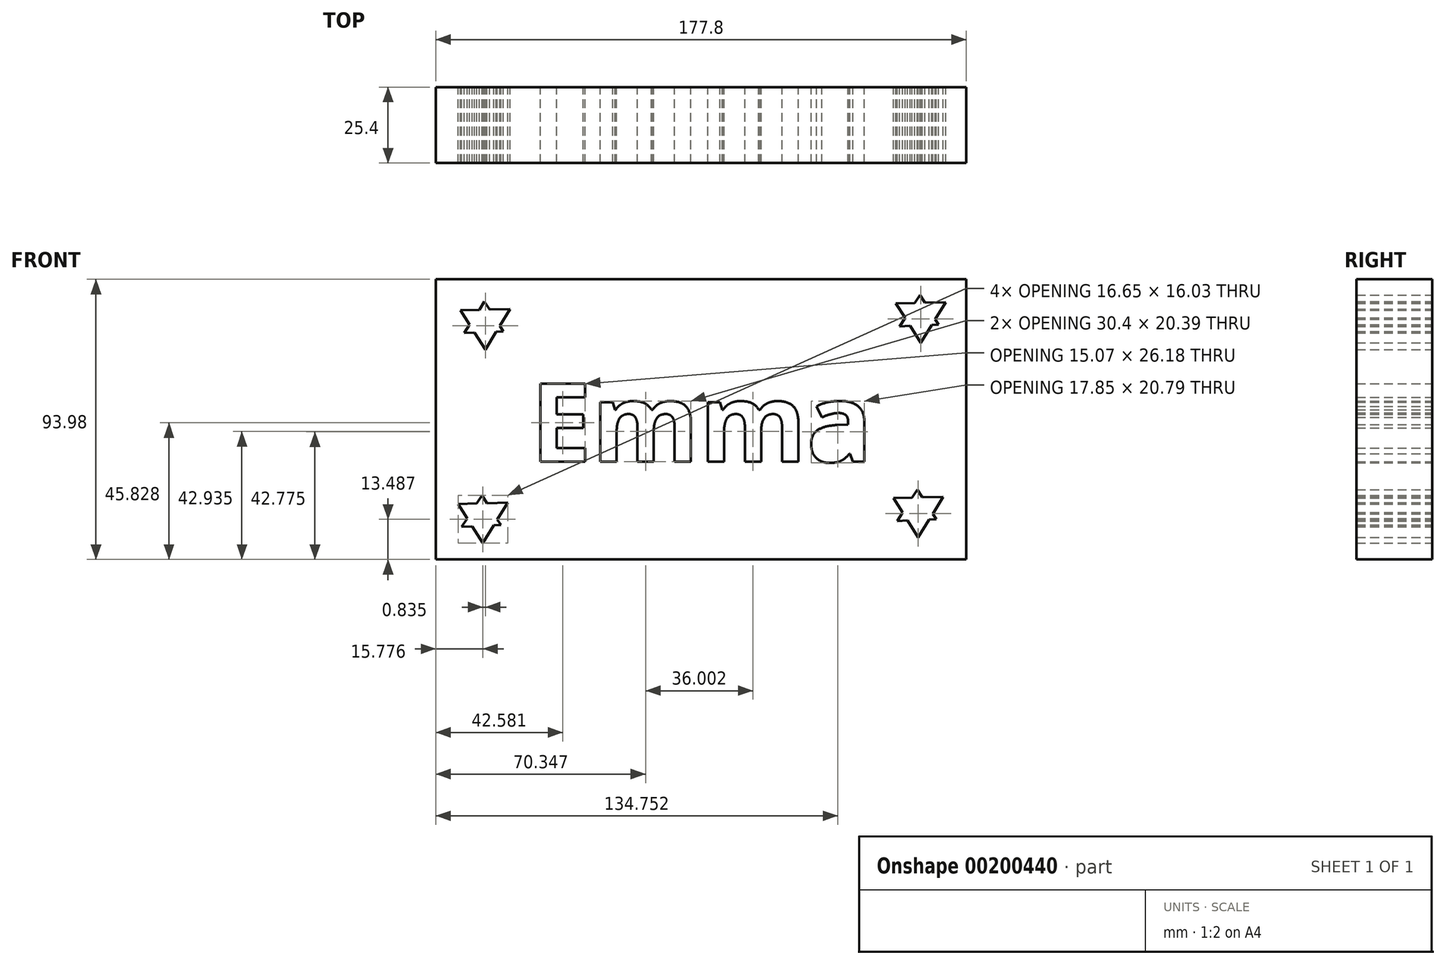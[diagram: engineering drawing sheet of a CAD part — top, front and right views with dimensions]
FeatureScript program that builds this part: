
annotation { "Feature Type Name" : "Feature", "Feature Type Description" : "" }
export const myFeature = defineFeature(function(context is Context, id is Id, definition is map)
    precondition{}
    {
        {
            var Q0;
            Q0=qCreatedBy(makeId("Front.planeOp"),FACE);
            var sketch = newSketch(context, id + "F0", { "sketchPlane" : qUnion([Q0])});
            skLineSegment(sketch, "E0.bottom", {"start": v(88.9, -46.99) * mm, "end": v(-88.9, -47) * mm});
            skLineSegment(sketch, "E0.top", {"start": v(88.9, 47) * mm, "end": v(-88.9, 46.99) * mm});
            skLineSegment(sketch, "E0.left", {"start": v(88.9, -47) * mm, "end": v(88.9, 47) * mm});
            skLineSegment(sketch, "E0.right", {"start": v(-88.9, -47) * mm, "end": v(-88.9, 46.99) * mm});
            skPoint(sketch, "E0.middle", {"position": v(0, 0) * mm});
            skText(sketch, "E1", { "text": "Emma", "fontName": "OpenSans-Bold.ttf"});
            skLineSegment(sketch, "E2", {"start": v(-80.61, 36.58) * mm, "end": v(-77.55, 31.75) * mm});
            skLineSegment(sketch, "E3", {"start": v(-72.29, 23.44) * mm, "end": v(-68.64, 29.4) * mm});
            skLineSegment(sketch, "E4", {"start": v(-63.96, 37.02) * mm, "end": v(-70.9, 36.84) * mm});
            skPoint(sketch, "E5.endSnap0", {"position": v(-76.45, 30.01) * mm});
            skLineSegment(sketch, "E6", {"start": v(-79.36, 28.96) * mm, "end": v(-77.55, 31.75) * mm});
            skLineSegment(sketch, "E7", {"start": v(-72.57, 39.47) * mm, "end": v(-70.9, 36.84) * mm});
            skLineSegment(sketch, "E8", {"start": v(-66.25, 29.5) * mm, "end": v(-68.64, 29.4) * mm});
            skLineSegment(sketch, "E9.trimOffspring", {"start": v(-74.33, 36.75) * mm, "end": v(-80.61, 36.58) * mm});
            skLineSegment(sketch, "E10.trimOffspring", {"start": v(-75.87, 29.1) * mm, "end": v(-72.29, 23.44) * mm});
            skLineSegment(sketch, "E11.trimOffspring", {"start": v(-67.43, 31.36) * mm, "end": v(-63.96, 37.02) * mm});
            skLineSegment(sketch, "E12.trimOffspring", {"start": v(-67.43, 31.36) * mm, "end": v(-66.25, 29.5) * mm});
            skLineSegment(sketch, "E13.trimOffspring", {"start": v(-74.33, 36.75) * mm, "end": v(-72.57, 39.47) * mm});
            skLineSegment(sketch, "E14.trimOffspring", {"start": v(-75.87, 29.1) * mm, "end": v(-79.36, 28.96) * mm});
            skLineSegment(sketch, "E15", {"start": v(65.35, 38.83) * mm, "end": v(68.41, 34) * mm});
            skLineSegment(sketch, "E16", {"start": v(73.68, 25.68) * mm, "end": v(77.33, 31.64) * mm});
            skLineSegment(sketch, "E17", {"start": v(82, 39.27) * mm, "end": v(75.06, 39.08) * mm});
            skPoint(sketch, "E18.endSnap0", {"position": v(69.51, 32.26) * mm});
            skLineSegment(sketch, "E19", {"start": v(66.6, 31.2) * mm, "end": v(68.41, 34) * mm});
            skLineSegment(sketch, "E20", {"start": v(73.4, 41.72) * mm, "end": v(75.06, 39.08) * mm});
            skLineSegment(sketch, "E21", {"start": v(79.72, 31.74) * mm, "end": v(77.33, 31.64) * mm});
            skLineSegment(sketch, "E22.trimOffspring", {"start": v(71.64, 39) * mm, "end": v(65.35, 38.83) * mm});
            skLineSegment(sketch, "E23.trimOffspring", {"start": v(70.1, 31.34) * mm, "end": v(73.68, 25.68) * mm});
            skLineSegment(sketch, "E24.trimOffspring", {"start": v(78.53, 33.6) * mm, "end": v(82, 39.27) * mm});
            skLineSegment(sketch, "E25.trimOffspring", {"start": v(78.53, 33.6) * mm, "end": v(79.72, 31.74) * mm});
            skLineSegment(sketch, "E26.trimOffspring", {"start": v(71.64, 39) * mm, "end": v(73.4, 41.72) * mm});
            skLineSegment(sketch, "E27.trimOffspring", {"start": v(70.1, 31.34) * mm, "end": v(66.6, 31.2) * mm});
            skLineSegment(sketch, "E28", {"start": v(-81.45, -28.38) * mm, "end": v(-78.39, -33.2) * mm});
            skLineSegment(sketch, "E29", {"start": v(-73.12, -41.52) * mm, "end": v(-69.47, -35.56) * mm});
            skLineSegment(sketch, "E30", {"start": v(-64.8, -27.94) * mm, "end": v(-71.74, -28.12) * mm});
            skPoint(sketch, "E31.endSnap0", {"position": v(-77.29, -34.95) * mm});
            skLineSegment(sketch, "E32", {"start": v(-80.2, -36) * mm, "end": v(-78.39, -33.2) * mm});
            skLineSegment(sketch, "E33", {"start": v(-73.4, -25.49) * mm, "end": v(-71.74, -28.12) * mm});
            skLineSegment(sketch, "E34", {"start": v(-67.08, -35.47) * mm, "end": v(-69.47, -35.56) * mm});
            skLineSegment(sketch, "E35.trimOffspring", {"start": v(-75.16, -28.2) * mm, "end": v(-81.45, -28.38) * mm});
            skLineSegment(sketch, "E36.trimOffspring", {"start": v(-76.7, -35.86) * mm, "end": v(-73.12, -41.52) * mm});
            skLineSegment(sketch, "E37.trimOffspring", {"start": v(-68.27, -33.6) * mm, "end": v(-64.8, -27.94) * mm});
            skLineSegment(sketch, "E38.trimOffspring", {"start": v(-68.27, -33.6) * mm, "end": v(-67.08, -35.47) * mm});
            skLineSegment(sketch, "E39.trimOffspring", {"start": v(-75.16, -28.2) * mm, "end": v(-73.4, -25.49) * mm});
            skLineSegment(sketch, "E40.trimOffspring", {"start": v(-76.7, -35.86) * mm, "end": v(-80.2, -36) * mm});
            skLineSegment(sketch, "E41", {"start": v(64.53, -26.45) * mm, "end": v(67.58, -31.28) * mm});
            skLineSegment(sketch, "E42", {"start": v(72.85, -39.6) * mm, "end": v(76.5, -33.64) * mm});
            skLineSegment(sketch, "E43", {"start": v(81.17, -26) * mm, "end": v(74.24, -26.2) * mm});
            skPoint(sketch, "E44.endSnap0", {"position": v(68.69, -33.02) * mm});
            skLineSegment(sketch, "E45", {"start": v(65.78, -34.07) * mm, "end": v(67.58, -31.28) * mm});
            skLineSegment(sketch, "E46", {"start": v(72.57, -23.56) * mm, "end": v(74.24, -26.2) * mm});
            skLineSegment(sketch, "E47", {"start": v(78.89, -33.54) * mm, "end": v(76.5, -33.64) * mm});
            skLineSegment(sketch, "E48.trimOffspring", {"start": v(70.8, -26.28) * mm, "end": v(64.53, -26.45) * mm});
            skLineSegment(sketch, "E49.trimOffspring", {"start": v(69.27, -33.93) * mm, "end": v(72.85, -39.6) * mm});
            skLineSegment(sketch, "E50.trimOffspring", {"start": v(77.7, -31.67) * mm, "end": v(81.17, -26) * mm});
            skLineSegment(sketch, "E51.trimOffspring", {"start": v(77.7, -31.67) * mm, "end": v(78.89, -33.54) * mm});
            skLineSegment(sketch, "E52.trimOffspring", {"start": v(70.8, -26.28) * mm, "end": v(72.57, -23.56) * mm});
            skLineSegment(sketch, "E53.trimOffspring", {"start": v(69.27, -33.93) * mm, "end": v(65.78, -34.07) * mm});
            const initialGuessF0  = {"E1": [-0.05715, -0.01425, 1, 0, 0.0264]};
            skSetInitialGuess(sketch, initialGuessF0);
            skSolve(sketch);
        }
        {
            var Q0;
            Q0 = qSketchRegion(id + "F0", true);
            extrude(context, id + "F1", {"entities" : qUnion([Q0]), "depth" : 25.4 * mm});
        }
    });
